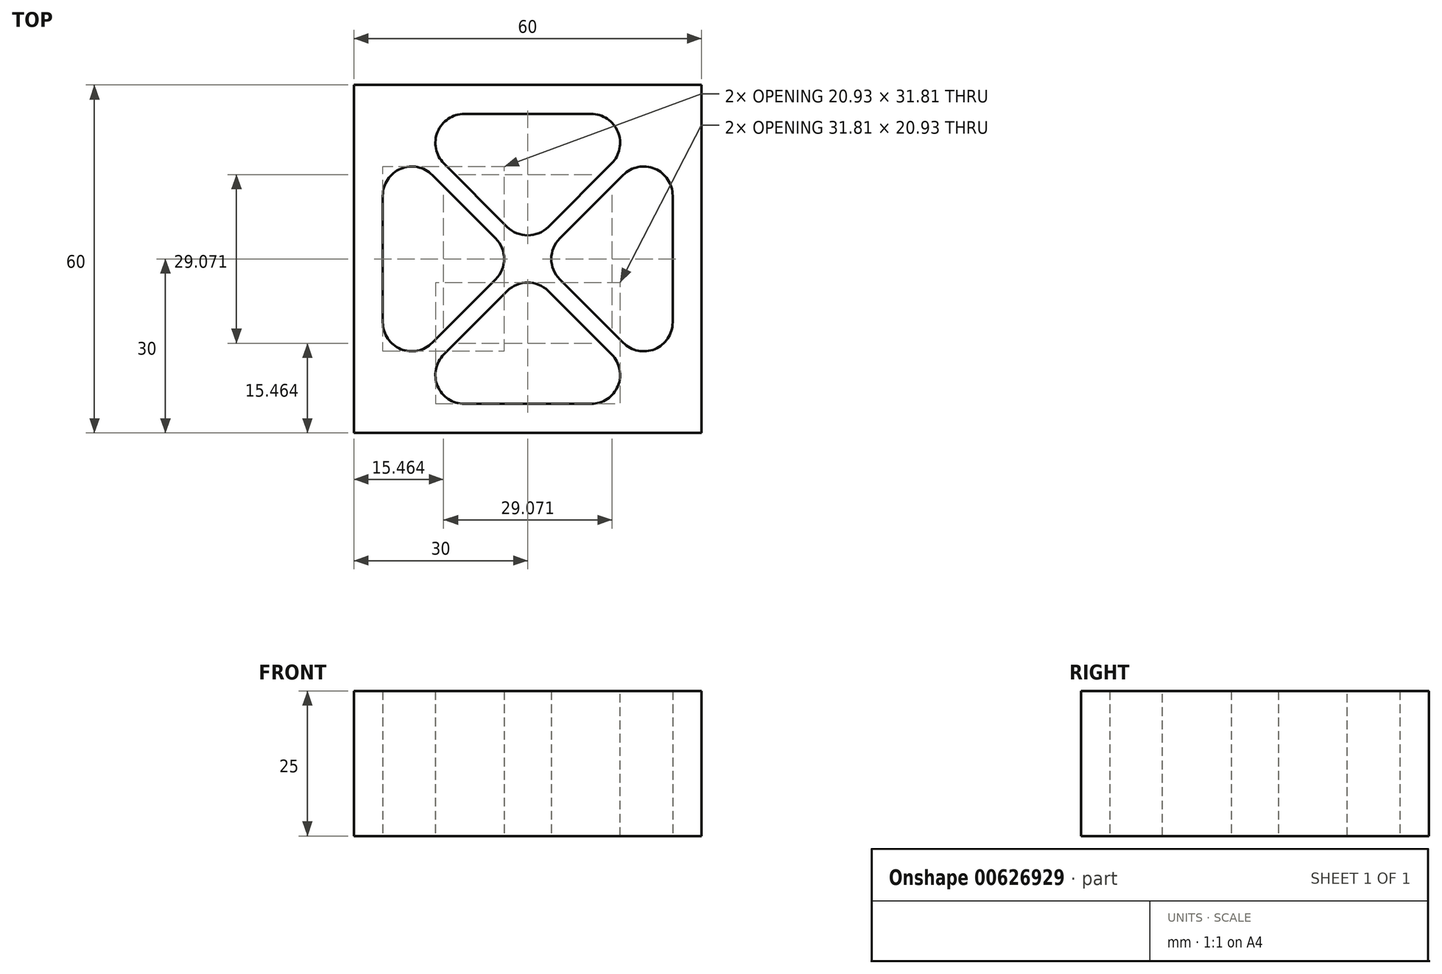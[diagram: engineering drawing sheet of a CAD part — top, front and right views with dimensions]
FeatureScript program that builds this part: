
annotation { "Feature Type Name" : "Feature", "Feature Type Description" : "" }
export const myFeature = defineFeature(function(context is Context, id is Id, definition is map)
    precondition{}
    {
        {
            var Q0;
            Q0=qCreatedBy(makeId("Top.planeOp"),FACE);
            var sketch = newSketch(context, id + "F0", { "sketchPlane" : qUnion([Q0])});
            skLineSegment(sketch, "E0.bottom", {"start": v(-25, 25) * mm, "end": v(25, 25) * mm});
            skLineSegment(sketch, "E0.top", {"start": v(-25, -25) * mm, "end": v(25, -25) * mm});
            skLineSegment(sketch, "E0.left", {"start": v(-25, 25) * mm, "end": v(-25, -25) * mm});
            skLineSegment(sketch, "E0.right", {"start": v(25, 25) * mm, "end": v(25, -25) * mm});
            skPoint(sketch, "E0.middle", {"position": v(0, 0) * mm});
            skLineSegment(sketch, "E1", {"start": v(23, -25) * mm, "end": v(3.54, -5.54) * mm});
            skLineSegment(sketch, "E2", {"start": v(25, -23) * mm, "end": v(5.54, -3.54) * mm});
            skLineSegment(sketch, "E3", {"start": v(-25, -23) * mm, "end": v(-5.54, -3.54) * mm});
            skLineSegment(sketch, "E4", {"start": v(-23, -25) * mm, "end": v(-3.54, -5.54) * mm});
            skLineSegment(sketch, "E5.trimOffspring", {"start": v(-3.54, 5.54) * mm, "end": v(-23, 25) * mm});
            skLineSegment(sketch, "E6.trimOffspring", {"start": v(3.54, 5.54) * mm, "end": v(23, 25) * mm});
            skLineSegment(sketch, "E7.trimOffspring", {"start": v(-5.54, 3.54) * mm, "end": v(-25, 23) * mm});
            skLineSegment(sketch, "E8.trimOffspring", {"start": v(5.54, 3.54) * mm, "end": v(25, 23) * mm});
            skPoint(sketch, "E9.visualSharp", {"position": v(0, -2) * mm});
            skArc(sketch, "E9.filletArc", {"start": v(3.54, -5.54) * mm, "mid": v(0, -4.07) * mm, "end": v(-3.54, -5.54) * mm});
            skPoint(sketch, "E10.visualSharp", {"position": v(2, 0) * mm});
            skArc(sketch, "E10.filletArc", {"start": v(5.54, 3.54) * mm, "mid": v(4.07, 0) * mm, "end": v(5.54, -3.54) * mm});
            skPoint(sketch, "E11.visualSharp", {"position": v(0, 2) * mm});
            skArc(sketch, "E11.filletArc", {"start": v(-3.54, 5.54) * mm, "mid": v(0, 4.07) * mm, "end": v(3.54, 5.54) * mm});
            skPoint(sketch, "E12.visualSharp", {"position": v(-2, 0) * mm});
            skArc(sketch, "E12.filletArc", {"start": v(-5.54, -3.54) * mm, "mid": v(-4.07, 0) * mm, "end": v(-5.54, 3.54) * mm});
            skLineSegment(sketch, "E13.bottom", {"start": v(30, -30) * mm, "end": v(-30, -30) * mm});
            skLineSegment(sketch, "E13.top", {"start": v(30, 30) * mm, "end": v(-30, 30) * mm});
            skLineSegment(sketch, "E13.left", {"start": v(30, -30) * mm, "end": v(30, 30) * mm});
            skLineSegment(sketch, "E13.right", {"start": v(-30, -30) * mm, "end": v(-30, 30) * mm});
            skSolve(sketch);
        }
        {
            var Q0;
            {var subQ0=sQuery(id+"F0.wireOp",EDGE,"E1");Q0=makeQuery(id+"F0.imprint","IMPRINT",FACE,{"disambiguationData":[TD([[makeQuery(id+"F0.imprint","IMPRINT",EDGE,{"derivedFrom":subQ0}),-1.0]])]});}
            var Q1;
            Q1=makeQuery(id+"F0.imprint","IMPRINT",FACE,{"disambiguationData":[TD([[makeQuery(id+"F0.imprint","IMPRINT",EDGE,{"derivedFrom":sQuery(id+"F0.wireOp",EDGE,"E13.bottom")}),-1.0]])]});
            extrude(context, id + "F1", {"entities" : qUnion([Q0, Q1]), "depth" : 25 * mm, "offsetDistance" : 25 * mm});
        }
        {
            var Q0;
            Q0=makeQuery(id+"F1.opExtrude","SWEPT_EDGE",EDGE,{"disambiguationData":[OSD([sQuery(id+"F0.wireOp",EDGE,"E0.bottom"),sQuery(id+"F0.wireOp",EDGE,"E5.trimOffspring")])]});
            var Q1;
            Q1=makeQuery(id+"F1.opExtrude","SWEPT_EDGE",EDGE,{"disambiguationData":[OSD([sQuery(id+"F0.wireOp",EDGE,"E0.left"),sQuery(id+"F0.wireOp",EDGE,"E7.trimOffspring")])]});
            var Q2;
            Q2=makeQuery(id+"F1.opExtrude","SWEPT_EDGE",EDGE,{"disambiguationData":[OSD([sQuery(id+"F0.wireOp",EDGE,"E0.bottom"),sQuery(id+"F0.wireOp",EDGE,"E6.trimOffspring")])]});
            var Q3;
            Q3=makeQuery(id+"F1.opExtrude","SWEPT_EDGE",EDGE,{"disambiguationData":[OSD([sQuery(id+"F0.wireOp",EDGE,"E0.right"),sQuery(id+"F0.wireOp",EDGE,"E8.trimOffspring")])]});
            var Q4;
            Q4=makeQuery(id+"F1.opExtrude","SWEPT_EDGE",EDGE,{"disambiguationData":[OSD([sQuery(id+"F0.wireOp",EDGE,"E0.top"),sQuery(id+"F0.wireOp",EDGE,"E4")])]});
            var Q5;
            Q5=makeQuery(id+"F1.opExtrude","SWEPT_EDGE",EDGE,{"disambiguationData":[OSD([sQuery(id+"F0.wireOp",EDGE,"E0.top"),sQuery(id+"F0.wireOp",EDGE,"E1")])]});
            var Q6;
            Q6=makeQuery(id+"F1.opExtrude","SWEPT_EDGE",EDGE,{"disambiguationData":[OSD([sQuery(id+"F0.wireOp",EDGE,"E0.right"),sQuery(id+"F0.wireOp",EDGE,"E2")])]});
            var Q7;
            Q7=makeQuery(id+"F1.opExtrude","SWEPT_EDGE",EDGE,{"disambiguationData":[OSD([sQuery(id+"F0.wireOp",EDGE,"E0.left"),sQuery(id+"F0.wireOp",EDGE,"E3")])]});
            fillet(context, id + "F2", {"entities" : qUnion([Q0, Q1, Q2, Q3, Q4, Q5, Q6, Q7]), "radius" : 5 * mm, "tangentPropagation" : true, "allowEdgeOverflow" : false});
        }
    });
